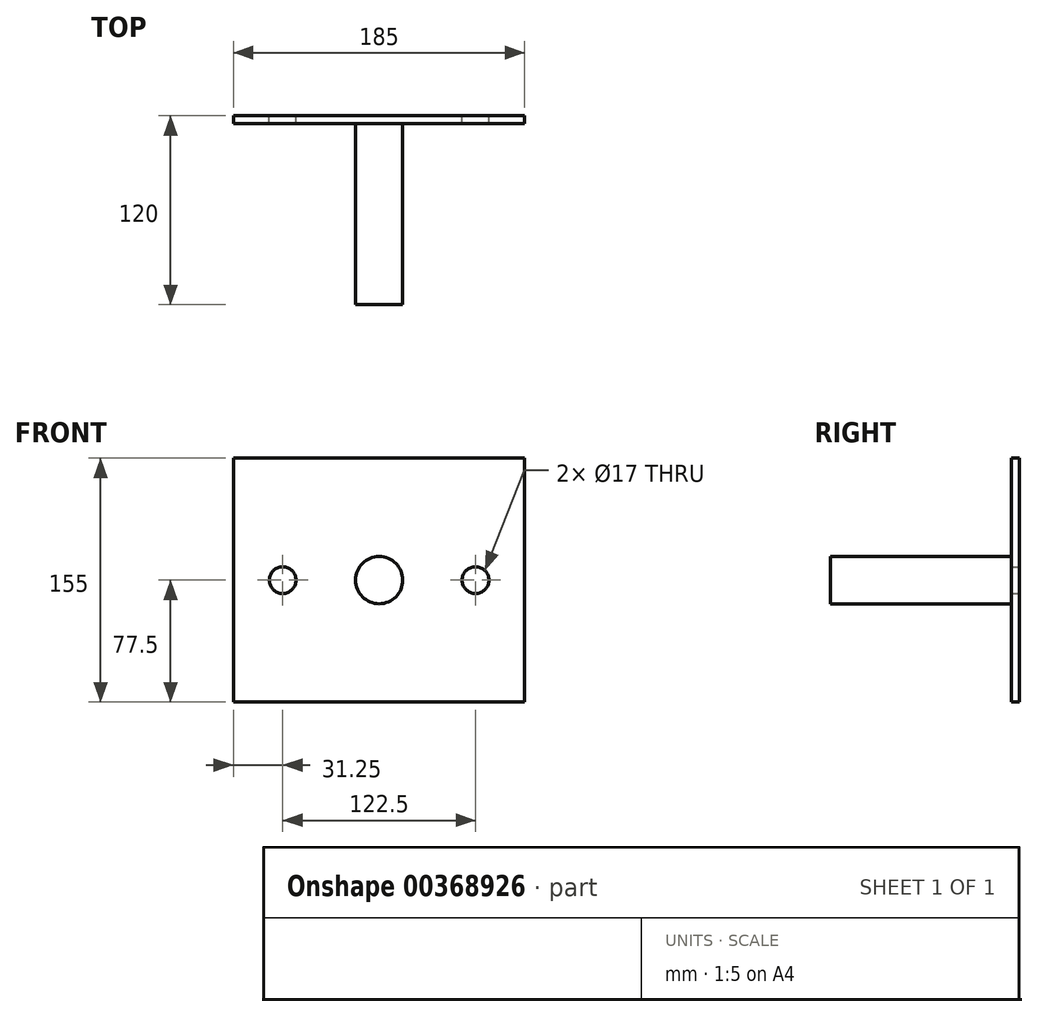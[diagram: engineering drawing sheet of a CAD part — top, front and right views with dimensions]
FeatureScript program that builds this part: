
annotation { "Feature Type Name" : "Feature", "Feature Type Description" : "" }
export const myFeature = defineFeature(function(context is Context, id is Id, definition is map)
    precondition{}
    {
        {
            var Q0;
            Q0=qCreatedBy(makeId("Front.planeOp"),FACE);
            var sketch = newSketch(context, id + "F0", { "sketchPlane" : qUnion([Q0])});
            skLineSegment(sketch, "E0.bottom", {"start": v(-92.5, 77.5) * mm, "end": v(92.5, 77.5) * mm});
            skLineSegment(sketch, "E0.top", {"start": v(-92.5, -77.5) * mm, "end": v(92.5, -77.5) * mm});
            skLineSegment(sketch, "E0.left", {"start": v(-92.5, 77.5) * mm, "end": v(-92.5, -77.5) * mm});
            skLineSegment(sketch, "E0.right", {"start": v(92.5, 77.5) * mm, "end": v(92.5, -77.5) * mm});
            skPoint(sketch, "E0.middle", {"position": v(0, 0) * mm});
            skCircle(sketch, "E1", {"center": v(0, 0) * mm, "radius": 15 * mm});
            skCircle(sketch, "E2", {"center": v(-61.25, 0) * mm, "radius": 8.5 * mm});
            skLineSegment(sketch, "E3", {"start": v(0, 0) * mm, "end": v(0, 91.07) * mm, "construction": true});
            skPoint(sketch, "E3.endSnap0", {"position": v(0, 77.5) * mm});
            skCircle(sketch, "E4.MirrorC", {"center": v(61.25, 0) * mm, "radius": 8.5 * mm});
            skSolve(sketch);
        }
        {
            var Q0;
            Q0=makeQuery(id+"F0.imprint","IMPRINT",FACE,{"disambiguationData":[TD([[makeQuery(id+"F0.imprint","IMPRINT",EDGE,{"derivedFrom":sQuery(id+"F0.wireOp",EDGE,"E1")}),1.0]])]});
            extrude(context, id + "F1", {"entities" : qUnion([Q0]), "depth" : 120 * mm});
        }
        {
            var Q0;
            Q0=makeQuery(id+"F0.imprint","IMPRINT",FACE,{"disambiguationData":[TD([[makeQuery(id+"F0.imprint","IMPRINT",EDGE,{"derivedFrom":sQuery(id+"F0.wireOp",EDGE,"E0.bottom")}),-1.0]])]});
            extrude(context, id + "F2", {"entities" : qUnion([Q0]), "operationType" : NewBodyOperationType.ADD, "depth" : 5 * mm});
        }
    });
